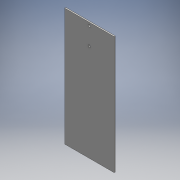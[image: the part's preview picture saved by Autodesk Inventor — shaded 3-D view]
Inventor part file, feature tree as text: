
AUTODESK INVENTOR PART (.ipt)
format: ipt  version: 2016 (Build 200138000, 138)  size: 98,816 bytes
history: native  units: mm
features: extrude x2, sketch x2, other x1
ambient origin geometry x8: Origin, YZ Plane, XZ Plane, XY Plane, X Axis, Y Axis, Z Axis, Center Point
bodies: Body1 (feature_tree)
feature tree (5):
  other  "ソリッド1"
  extrude  "押し出し1"  Depth=84.0mm
  extrude  "押し出し2"  Depth=200.0mm
  sketch  "スケッチ1"
  sketch  "スケッチ2"
